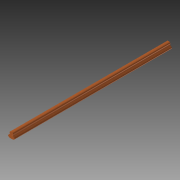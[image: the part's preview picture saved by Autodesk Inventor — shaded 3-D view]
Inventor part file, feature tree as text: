
AUTODESK INVENTOR PART (.ipt)
format: ipt  version: 2015 (Build 190159000, 159)  size: 91,136 bytes
history: native  units: in
note: dims shown in document units (in); Inventor stores cm internally (conversion verified against a paired STEP export)
features: extrude x1, sketch x1
ambient origin geometry x8: Origin, YZ Plane, XZ Plane, XY Plane, X Axis, Y Axis, Z Axis, Center Point
bodies: Solid1 (feature_tree)
feature tree (2):
  extrude  "Extrusion1"  Depth=0.6in
  sketch  "Sketch1"  dims[d0=1.0in d2=0.6in d3=0.5in d9=0.1in d10=0.1in d11=1.0in d13=0.25in d14=0.5in d15=0.5in d16=0.5in d17=0.25in d18=54.22in d19=0.0in]
